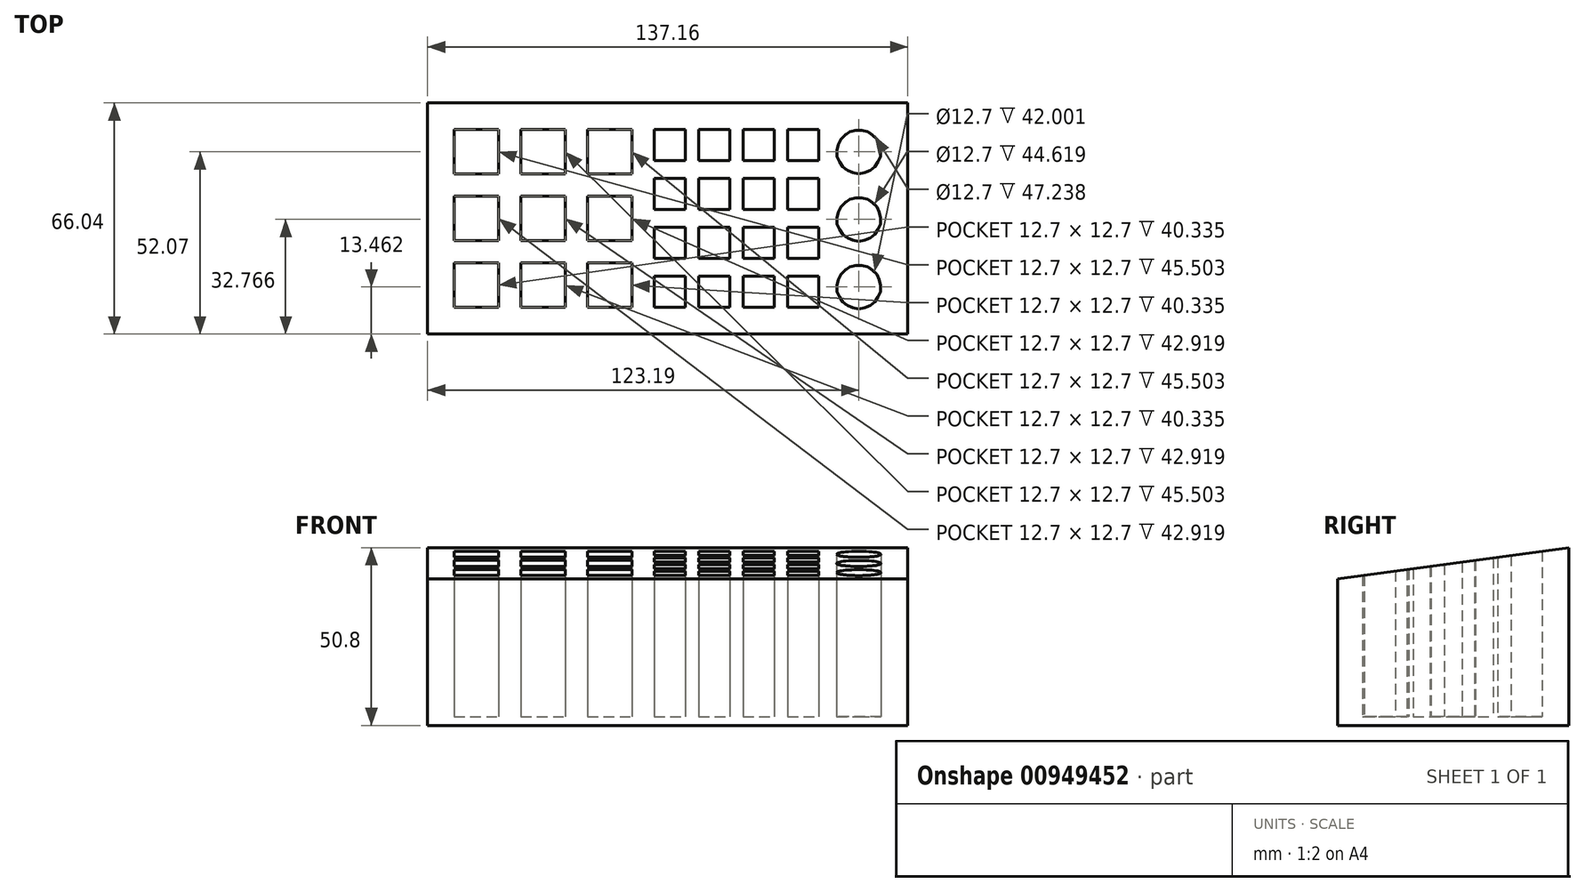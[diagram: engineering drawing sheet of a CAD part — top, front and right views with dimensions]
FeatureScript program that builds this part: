
annotation { "Feature Type Name" : "Feature", "Feature Type Description" : "" }
export const myFeature = defineFeature(function(context is Context, id is Id, definition is map)
    precondition{}
    {
        {
            var Q0;
            Q0=qCreatedBy(makeId("Top.planeOp"),FACE);
            var sketch = newSketch(context, id + "F0", { "sketchPlane" : qUnion([Q0])});
            skLineSegment(sketch, "E0.bottom", {"start": v(-57.15, 6.35) * mm, "end": v(-44.45, 6.35) * mm});
            skLineSegment(sketch, "E0.top", {"start": v(-57.15, -6.35) * mm, "end": v(-44.45, -6.35) * mm});
            skLineSegment(sketch, "E0.left", {"start": v(-57.15, 6.35) * mm, "end": v(-57.15, -6.35) * mm});
            skLineSegment(sketch, "E0.right", {"start": v(-44.45, 6.35) * mm, "end": v(-44.45, -6.35) * mm});
            skPoint(sketch, "E0.middle", {"position": v(-50.8, 0) * mm});
            skLineSegment(sketch, "E1.0.1.0", {"start": v(-57.15, -12.7) * mm, "end": v(-44.45, -12.7) * mm});
            skLineSegment(sketch, "E1.0.1.1", {"start": v(-57.15, -12.7) * mm, "end": v(-57.15, -25.4) * mm});
            skLineSegment(sketch, "E1.0.1.2", {"start": v(-57.15, -25.4) * mm, "end": v(-44.45, -25.4) * mm});
            skLineSegment(sketch, "E1.0.1.3", {"start": v(-44.45, -12.7) * mm, "end": v(-44.45, -25.4) * mm});
            skLineSegment(sketch, "E1.0.2.0", {"start": v(-57.15, -31.75) * mm, "end": v(-44.45, -31.75) * mm});
            skLineSegment(sketch, "E1.0.2.1", {"start": v(-57.15, -31.75) * mm, "end": v(-57.15, -44.45) * mm});
            skLineSegment(sketch, "E1.0.2.2", {"start": v(-57.15, -44.45) * mm, "end": v(-44.45, -44.45) * mm});
            skLineSegment(sketch, "E1.0.2.3", {"start": v(-44.45, -31.75) * mm, "end": v(-44.45, -44.45) * mm});
            skLineSegment(sketch, "E1.1.0.0", {"start": v(-38.1, 6.35) * mm, "end": v(-25.4, 6.35) * mm});
            skLineSegment(sketch, "E1.1.0.1", {"start": v(-38.1, 6.35) * mm, "end": v(-38.1, -6.35) * mm});
            skLineSegment(sketch, "E1.1.0.2", {"start": v(-38.1, -6.35) * mm, "end": v(-25.4, -6.35) * mm});
            skLineSegment(sketch, "E1.1.0.3", {"start": v(-25.4, 6.35) * mm, "end": v(-25.4, -6.35) * mm});
            skLineSegment(sketch, "E1.1.1.0", {"start": v(-38.1, -12.7) * mm, "end": v(-25.4, -12.7) * mm});
            skLineSegment(sketch, "E1.1.1.1", {"start": v(-38.1, -12.7) * mm, "end": v(-38.1, -25.4) * mm});
            skLineSegment(sketch, "E1.1.1.2", {"start": v(-38.1, -25.4) * mm, "end": v(-25.4, -25.4) * mm});
            skLineSegment(sketch, "E1.1.1.3", {"start": v(-25.4, -12.7) * mm, "end": v(-25.4, -25.4) * mm});
            skLineSegment(sketch, "E1.1.2.0", {"start": v(-38.1, -31.75) * mm, "end": v(-25.4, -31.75) * mm});
            skLineSegment(sketch, "E1.1.2.1", {"start": v(-38.1, -31.75) * mm, "end": v(-38.1, -44.45) * mm});
            skLineSegment(sketch, "E1.1.2.2", {"start": v(-38.1, -44.45) * mm, "end": v(-25.4, -44.45) * mm});
            skLineSegment(sketch, "E1.1.2.3", {"start": v(-25.4, -31.75) * mm, "end": v(-25.4, -44.45) * mm});
            skLineSegment(sketch, "E1.2.0.0", {"start": v(-19.05, 6.35) * mm, "end": v(-6.35, 6.35) * mm});
            skLineSegment(sketch, "E1.2.0.1", {"start": v(-19.05, 6.35) * mm, "end": v(-19.05, -6.35) * mm});
            skLineSegment(sketch, "E1.2.0.2", {"start": v(-19.05, -6.35) * mm, "end": v(-6.35, -6.35) * mm});
            skLineSegment(sketch, "E1.2.0.3", {"start": v(-6.35, 6.35) * mm, "end": v(-6.35, -6.35) * mm});
            skLineSegment(sketch, "E1.2.1.0", {"start": v(-19.05, -12.7) * mm, "end": v(-6.35, -12.7) * mm});
            skLineSegment(sketch, "E1.2.1.1", {"start": v(-19.05, -12.7) * mm, "end": v(-19.05, -25.4) * mm});
            skLineSegment(sketch, "E1.2.1.2", {"start": v(-19.05, -25.4) * mm, "end": v(-6.35, -25.4) * mm});
            skLineSegment(sketch, "E1.2.1.3", {"start": v(-6.35, -12.7) * mm, "end": v(-6.35, -25.4) * mm});
            skLineSegment(sketch, "E1.2.2.0", {"start": v(-19.05, -31.75) * mm, "end": v(-6.35, -31.75) * mm});
            skLineSegment(sketch, "E1.2.2.1", {"start": v(-19.05, -31.75) * mm, "end": v(-19.05, -44.45) * mm});
            skLineSegment(sketch, "E1.2.2.2", {"start": v(-19.05, -44.45) * mm, "end": v(-6.35, -44.45) * mm});
            skLineSegment(sketch, "E1.2.2.3", {"start": v(-6.35, -31.75) * mm, "end": v(-6.35, -44.45) * mm});
            skLineSegment(sketch, "E1.direction1", {"start": v(-57.15, 6.35) * mm, "end": v(-38.1, 6.35) * mm, "construction": true});
            skLineSegment(sketch, "E1.direction2", {"start": v(-57.15, 6.35) * mm, "end": v(-57.15, -12.7) * mm, "construction": true});
            skLineSegment(sketch, "E2.bottom", {"start": v(0, -44.45) * mm, "end": v(8.9, -44.45) * mm});
            skLineSegment(sketch, "E2.top", {"start": v(0, -35.56) * mm, "end": v(8.89, -35.56) * mm});
            skLineSegment(sketch, "E2.left", {"start": v(0, -44.45) * mm, "end": v(0, -35.56) * mm});
            skLineSegment(sketch, "E2.right", {"start": v(8.9, -44.45) * mm, "end": v(8.89, -35.56) * mm});
            skLineSegment(sketch, "E3.0.1.0", {"start": v(0, -30.48) * mm, "end": v(0, -21.59) * mm});
            skLineSegment(sketch, "E3.0.1.1", {"start": v(0, -30.48) * mm, "end": v(8.9, -30.48) * mm});
            skLineSegment(sketch, "E3.0.1.2", {"start": v(8.9, -30.48) * mm, "end": v(8.89, -21.59) * mm});
            skLineSegment(sketch, "E3.0.1.3", {"start": v(0, -21.59) * mm, "end": v(8.89, -21.59) * mm});
            skLineSegment(sketch, "E3.0.2.0", {"start": v(0, -16.5) * mm, "end": v(0, -7.62) * mm});
            skLineSegment(sketch, "E3.0.2.1", {"start": v(0, -16.5) * mm, "end": v(8.9, -16.5) * mm});
            skLineSegment(sketch, "E3.0.2.2", {"start": v(8.9, -16.51) * mm, "end": v(8.89, -7.62) * mm});
            skLineSegment(sketch, "E3.0.2.3", {"start": v(0, -7.62) * mm, "end": v(8.89, -7.62) * mm});
            skLineSegment(sketch, "E3.0.3.0", {"start": v(0, -2.54) * mm, "end": v(0, 6.35) * mm});
            skLineSegment(sketch, "E3.0.3.1", {"start": v(0, -2.54) * mm, "end": v(8.9, -2.54) * mm});
            skLineSegment(sketch, "E3.0.3.2", {"start": v(8.9, -2.54) * mm, "end": v(8.89, 6.35) * mm});
            skLineSegment(sketch, "E3.0.3.3", {"start": v(0, 6.35) * mm, "end": v(8.89, 6.35) * mm});
            skLineSegment(sketch, "E3.1.0.0", {"start": v(12.7, -44.45) * mm, "end": v(12.7, -35.56) * mm});
            skLineSegment(sketch, "E3.1.0.1", {"start": v(12.7, -44.45) * mm, "end": v(21.59, -44.45) * mm});
            skLineSegment(sketch, "E3.1.0.2", {"start": v(21.59, -44.45) * mm, "end": v(21.59, -35.56) * mm});
            skLineSegment(sketch, "E3.1.0.3", {"start": v(12.7, -35.56) * mm, "end": v(21.59, -35.56) * mm});
            skLineSegment(sketch, "E3.1.1.0", {"start": v(12.7, -30.48) * mm, "end": v(12.7, -21.59) * mm});
            skLineSegment(sketch, "E3.1.1.1", {"start": v(12.7, -30.48) * mm, "end": v(21.59, -30.48) * mm});
            skLineSegment(sketch, "E3.1.1.2", {"start": v(21.59, -30.48) * mm, "end": v(21.59, -21.59) * mm});
            skLineSegment(sketch, "E3.1.1.3", {"start": v(12.7, -21.59) * mm, "end": v(21.59, -21.59) * mm});
            skLineSegment(sketch, "E3.1.2.0", {"start": v(12.7, -16.5) * mm, "end": v(12.7, -7.62) * mm});
            skLineSegment(sketch, "E3.1.2.1", {"start": v(12.7, -16.5) * mm, "end": v(21.59, -16.5) * mm});
            skLineSegment(sketch, "E3.1.2.2", {"start": v(21.59, -16.51) * mm, "end": v(21.59, -7.62) * mm});
            skLineSegment(sketch, "E3.1.2.3", {"start": v(12.7, -7.62) * mm, "end": v(21.59, -7.62) * mm});
            skLineSegment(sketch, "E3.1.3.0", {"start": v(12.7, -2.54) * mm, "end": v(12.7, 6.35) * mm});
            skLineSegment(sketch, "E3.1.3.1", {"start": v(12.7, -2.54) * mm, "end": v(21.59, -2.54) * mm});
            skLineSegment(sketch, "E3.1.3.2", {"start": v(21.59, -2.54) * mm, "end": v(21.59, 6.35) * mm});
            skLineSegment(sketch, "E3.1.3.3", {"start": v(12.7, 6.35) * mm, "end": v(21.59, 6.35) * mm});
            skLineSegment(sketch, "E3.2.0.0", {"start": v(25.4, -44.45) * mm, "end": v(25.4, -35.56) * mm});
            skLineSegment(sketch, "E3.2.0.1", {"start": v(25.4, -44.45) * mm, "end": v(34.3, -44.45) * mm});
            skLineSegment(sketch, "E3.2.0.2", {"start": v(34.3, -44.45) * mm, "end": v(34.3, -35.56) * mm});
            skLineSegment(sketch, "E3.2.0.3", {"start": v(25.4, -35.56) * mm, "end": v(34.3, -35.56) * mm});
            skLineSegment(sketch, "E3.2.1.0", {"start": v(25.4, -30.48) * mm, "end": v(25.4, -21.59) * mm});
            skLineSegment(sketch, "E3.2.1.1", {"start": v(25.4, -30.48) * mm, "end": v(34.29, -30.48) * mm});
            skLineSegment(sketch, "E3.2.1.2", {"start": v(34.3, -30.48) * mm, "end": v(34.3, -21.59) * mm});
            skLineSegment(sketch, "E3.2.1.3", {"start": v(25.4, -21.59) * mm, "end": v(34.29, -21.59) * mm});
            skLineSegment(sketch, "E3.2.2.0", {"start": v(25.4, -16.5) * mm, "end": v(25.4, -7.62) * mm});
            skLineSegment(sketch, "E3.2.2.1", {"start": v(25.4, -16.5) * mm, "end": v(34.29, -16.5) * mm});
            skLineSegment(sketch, "E3.2.2.2", {"start": v(34.3, -16.51) * mm, "end": v(34.3, -7.62) * mm});
            skLineSegment(sketch, "E3.2.2.3", {"start": v(25.4, -7.62) * mm, "end": v(34.29, -7.62) * mm});
            skLineSegment(sketch, "E3.2.3.0", {"start": v(25.4, -2.54) * mm, "end": v(25.4, 6.35) * mm});
            skLineSegment(sketch, "E3.2.3.1", {"start": v(25.4, -2.54) * mm, "end": v(34.29, -2.54) * mm});
            skLineSegment(sketch, "E3.2.3.2", {"start": v(34.3, -2.54) * mm, "end": v(34.3, 6.35) * mm});
            skLineSegment(sketch, "E3.2.3.3", {"start": v(25.4, 6.35) * mm, "end": v(34.29, 6.35) * mm});
            skLineSegment(sketch, "E3.3.0.0", {"start": v(38.1, -44.45) * mm, "end": v(38.1, -35.56) * mm});
            skLineSegment(sketch, "E3.3.0.1", {"start": v(38.1, -44.45) * mm, "end": v(47, -44.45) * mm});
            skLineSegment(sketch, "E3.3.0.2", {"start": v(47, -44.45) * mm, "end": v(47, -35.56) * mm});
            skLineSegment(sketch, "E3.3.0.3", {"start": v(38.1, -35.56) * mm, "end": v(46.99, -35.56) * mm});
            skLineSegment(sketch, "E3.3.1.0", {"start": v(38.1, -30.48) * mm, "end": v(38.1, -21.59) * mm});
            skLineSegment(sketch, "E3.3.1.1", {"start": v(38.1, -30.48) * mm, "end": v(46.99, -30.48) * mm});
            skLineSegment(sketch, "E3.3.1.2", {"start": v(47, -30.48) * mm, "end": v(47, -21.59) * mm});
            skLineSegment(sketch, "E3.3.1.3", {"start": v(38.1, -21.59) * mm, "end": v(46.99, -21.59) * mm});
            skLineSegment(sketch, "E3.3.2.0", {"start": v(38.1, -16.5) * mm, "end": v(38.1, -7.62) * mm});
            skLineSegment(sketch, "E3.3.2.1", {"start": v(38.1, -16.5) * mm, "end": v(46.99, -16.5) * mm});
            skLineSegment(sketch, "E3.3.2.2", {"start": v(47, -16.51) * mm, "end": v(47, -7.62) * mm});
            skLineSegment(sketch, "E3.3.2.3", {"start": v(38.1, -7.62) * mm, "end": v(46.99, -7.62) * mm});
            skLineSegment(sketch, "E3.3.3.0", {"start": v(38.1, -2.54) * mm, "end": v(38.1, 6.35) * mm});
            skLineSegment(sketch, "E3.3.3.1", {"start": v(38.1, -2.54) * mm, "end": v(46.99, -2.54) * mm});
            skLineSegment(sketch, "E3.3.3.2", {"start": v(47, -2.54) * mm, "end": v(47, 6.35) * mm});
            skLineSegment(sketch, "E3.3.3.3", {"start": v(38.1, 6.35) * mm, "end": v(46.99, 6.35) * mm});
            skLineSegment(sketch, "E3.direction1", {"start": v(0, -44.45) * mm, "end": v(12.7, -44.45) * mm, "construction": true});
            skLineSegment(sketch, "E3.direction2", {"start": v(0, -44.45) * mm, "end": v(0, -30.48) * mm, "construction": true});
            skCircle(sketch, "E4", {"center": v(58.42, 0) * mm, "radius": 6.35 * mm});
            skCircle(sketch, "E5.0.1.0", {"center": v(58.42, -19.3) * mm, "radius": 6.35 * mm});
            skCircle(sketch, "E5.0.2.0", {"center": v(58.42, -38.6) * mm, "radius": 6.35 * mm});
            skLineSegment(sketch, "E5.direction1", {"start": v(58.42, 0) * mm, "end": v(78.43, 0) * mm, "construction": true});
            skLineSegment(sketch, "E5.direction2", {"start": v(58.42, 0) * mm, "end": v(58.42, -19.3) * mm, "construction": true});
            skLineSegment(sketch, "E6.bottom", {"start": v(-64.77, 13.97) * mm, "end": v(72.39, 13.97) * mm});
            skLineSegment(sketch, "E6.top", {"start": v(-64.77, -52.07) * mm, "end": v(72.39, -52.07) * mm});
            skLineSegment(sketch, "E6.left", {"start": v(-64.77, 13.97) * mm, "end": v(-64.77, -52.07) * mm});
            skLineSegment(sketch, "E6.right", {"start": v(72.39, 13.97) * mm, "end": v(72.39, -52.07) * mm});
            skSolve(sketch);
        }
        {
            var Q0;
            Q0=makeQuery(id+"F0.imprint","IMPRINT",FACE,{"disambiguationData":[TD([[makeQuery(id+"F0.imprint","IMPRINT",EDGE,{"derivedFrom":sQuery(id+"F0.wireOp",EDGE,"E0.bottom")}),1.0]])]});
            extrude(context, id + "F1", {"entities" : qUnion([Q0]), "depth" : 50.8 * mm, "offsetDistance" : 25.4 * mm});
        }
        {
            var Q0;
            Q0=makeQuery(id+"F0.imprint","IMPRINT",FACE,{"disambiguationData":[TD([[makeQuery(id+"F0.imprint","IMPRINT",EDGE,{"derivedFrom":sQuery(id+"F0.wireOp",EDGE,"E0.bottom")}),-1.0]])]});
            var Q1;
            Q1=makeQuery(id+"F0.imprint","IMPRINT",FACE,{"disambiguationData":[TD([[makeQuery(id+"F0.imprint","IMPRINT",EDGE,{"derivedFrom":sQuery(id+"F0.wireOp",EDGE,"E1.1.0.0")}),-1.0]])]});
            var Q2;
            Q2=makeQuery(id+"F0.imprint","IMPRINT",FACE,{"disambiguationData":[TD([[makeQuery(id+"F0.imprint","IMPRINT",EDGE,{"derivedFrom":sQuery(id+"F0.wireOp",EDGE,"E1.0.1.0")}),-1.0]])]});
            var Q3;
            Q3=makeQuery(id+"F0.imprint","IMPRINT",FACE,{"disambiguationData":[TD([[makeQuery(id+"F0.imprint","IMPRINT",EDGE,{"derivedFrom":sQuery(id+"F0.wireOp",EDGE,"E1.1.1.0")}),-1.0]])]});
            var Q4;
            Q4=makeQuery(id+"F0.imprint","IMPRINT",FACE,{"disambiguationData":[TD([[makeQuery(id+"F0.imprint","IMPRINT",EDGE,{"derivedFrom":sQuery(id+"F0.wireOp",EDGE,"E1.0.2.0")}),-1.0]])]});
            var Q5;
            Q5=makeQuery(id+"F0.imprint","IMPRINT",FACE,{"disambiguationData":[TD([[makeQuery(id+"F0.imprint","IMPRINT",EDGE,{"derivedFrom":sQuery(id+"F0.wireOp",EDGE,"E1.1.2.0")}),-1.0]])]});
            var Q6;
            Q6=makeQuery(id+"F0.imprint","IMPRINT",FACE,{"disambiguationData":[TD([[makeQuery(id+"F0.imprint","IMPRINT",EDGE,{"derivedFrom":sQuery(id+"F0.wireOp",EDGE,"E1.2.2.0")}),-1.0]])]});
            var Q7;
            Q7=makeQuery(id+"F0.imprint","IMPRINT",FACE,{"disambiguationData":[TD([[makeQuery(id+"F0.imprint","IMPRINT",EDGE,{"derivedFrom":sQuery(id+"F0.wireOp",EDGE,"E1.2.1.0")}),-1.0]])]});
            var Q8;
            Q8=makeQuery(id+"F0.imprint","IMPRINT",FACE,{"disambiguationData":[TD([[makeQuery(id+"F0.imprint","IMPRINT",EDGE,{"derivedFrom":sQuery(id+"F0.wireOp",EDGE,"E1.2.0.0")}),-1.0]])]});
            var Q9;
            Q9=makeQuery(id+"F0.imprint","IMPRINT",FACE,{"disambiguationData":[TD([[makeQuery(id+"F0.imprint","IMPRINT",EDGE,{"derivedFrom":sQuery(id+"F0.wireOp",EDGE,"E3.0.3.0")}),-1.0]])]});
            var Q10;
            Q10=makeQuery(id+"F0.imprint","IMPRINT",FACE,{"disambiguationData":[TD([[makeQuery(id+"F0.imprint","IMPRINT",EDGE,{"derivedFrom":sQuery(id+"F0.wireOp",EDGE,"E3.0.2.0")}),-1.0]])]});
            var Q11;
            Q11=makeQuery(id+"F0.imprint","IMPRINT",FACE,{"disambiguationData":[TD([[makeQuery(id+"F0.imprint","IMPRINT",EDGE,{"derivedFrom":sQuery(id+"F0.wireOp",EDGE,"E3.0.1.0")}),-1.0]])]});
            var Q12;
            Q12=makeQuery(id+"F0.imprint","IMPRINT",FACE,{"disambiguationData":[TD([[makeQuery(id+"F0.imprint","IMPRINT",EDGE,{"derivedFrom":sQuery(id+"F0.wireOp",EDGE,"E2.bottom")}),1.0]])]});
            var Q13;
            Q13=makeQuery(id+"F0.imprint","IMPRINT",FACE,{"disambiguationData":[TD([[makeQuery(id+"F0.imprint","IMPRINT",EDGE,{"derivedFrom":sQuery(id+"F0.wireOp",EDGE,"E3.1.0.0")}),-1.0]])]});
            var Q14;
            Q14=makeQuery(id+"F0.imprint","IMPRINT",FACE,{"disambiguationData":[TD([[makeQuery(id+"F0.imprint","IMPRINT",EDGE,{"derivedFrom":sQuery(id+"F0.wireOp",EDGE,"E3.1.1.0")}),-1.0]])]});
            var Q15;
            Q15=makeQuery(id+"F0.imprint","IMPRINT",FACE,{"disambiguationData":[TD([[makeQuery(id+"F0.imprint","IMPRINT",EDGE,{"derivedFrom":sQuery(id+"F0.wireOp",EDGE,"E3.1.2.0")}),-1.0]])]});
            var Q16;
            Q16=makeQuery(id+"F0.imprint","IMPRINT",FACE,{"disambiguationData":[TD([[makeQuery(id+"F0.imprint","IMPRINT",EDGE,{"derivedFrom":sQuery(id+"F0.wireOp",EDGE,"E3.1.3.0")}),-1.0]])]});
            var Q17;
            Q17=makeQuery(id+"F0.imprint","IMPRINT",FACE,{"disambiguationData":[TD([[makeQuery(id+"F0.imprint","IMPRINT",EDGE,{"derivedFrom":sQuery(id+"F0.wireOp",EDGE,"E3.2.3.0")}),-1.0]])]});
            var Q18;
            Q18=makeQuery(id+"F0.imprint","IMPRINT",FACE,{"disambiguationData":[TD([[makeQuery(id+"F0.imprint","IMPRINT",EDGE,{"derivedFrom":sQuery(id+"F0.wireOp",EDGE,"E3.3.3.0")}),-1.0]])]});
            var Q19;
            Q19=makeQuery(id+"F0.imprint","IMPRINT",FACE,{"disambiguationData":[TD([[makeQuery(id+"F0.imprint","IMPRINT",EDGE,{"derivedFrom":sQuery(id+"F0.wireOp",EDGE,"E3.3.2.0")}),-1.0]])]});
            var Q20;
            Q20=makeQuery(id+"F0.imprint","IMPRINT",FACE,{"disambiguationData":[TD([[makeQuery(id+"F0.imprint","IMPRINT",EDGE,{"derivedFrom":sQuery(id+"F0.wireOp",EDGE,"E3.2.2.0")}),-1.0]])]});
            var Q21;
            Q21=makeQuery(id+"F0.imprint","IMPRINT",FACE,{"disambiguationData":[TD([[makeQuery(id+"F0.imprint","IMPRINT",EDGE,{"derivedFrom":sQuery(id+"F0.wireOp",EDGE,"E3.2.1.0")}),-1.0]])]});
            var Q22;
            Q22=makeQuery(id+"F0.imprint","IMPRINT",FACE,{"disambiguationData":[TD([[makeQuery(id+"F0.imprint","IMPRINT",EDGE,{"derivedFrom":sQuery(id+"F0.wireOp",EDGE,"E3.3.1.0")}),-1.0]])]});
            var Q23;
            Q23=makeQuery(id+"F0.imprint","IMPRINT",FACE,{"disambiguationData":[TD([[makeQuery(id+"F0.imprint","IMPRINT",EDGE,{"derivedFrom":sQuery(id+"F0.wireOp",EDGE,"E3.2.0.0")}),-1.0]])]});
            var Q24;
            Q24=makeQuery(id+"F0.imprint","IMPRINT",FACE,{"disambiguationData":[TD([[makeQuery(id+"F0.imprint","IMPRINT",EDGE,{"derivedFrom":sQuery(id+"F0.wireOp",EDGE,"E3.3.0.0")}),-1.0]])]});
            var Q25;
            Q25=makeQuery(id+"F0.imprint","IMPRINT",FACE,{"disambiguationData":[TD([[makeQuery(id+"F0.imprint","IMPRINT",EDGE,{"derivedFrom":sQuery(id+"F0.wireOp",EDGE,"E5.0.2.0")}),1.0]])]});
            var Q26;
            Q26=makeQuery(id+"F0.imprint","IMPRINT",FACE,{"disambiguationData":[TD([[makeQuery(id+"F0.imprint","IMPRINT",EDGE,{"derivedFrom":sQuery(id+"F0.wireOp",EDGE,"E5.0.1.0")}),1.0]])]});
            var Q27;
            Q27=makeQuery(id+"F0.imprint","IMPRINT",FACE,{"disambiguationData":[TD([[makeQuery(id+"F0.imprint","IMPRINT",EDGE,{"derivedFrom":sQuery(id+"F0.wireOp",EDGE,"E4")}),1.0]])]});
            extrude(context, id + "F2", {"entities" : qUnion([Q0, Q1, Q2, Q3, Q4, Q5, Q6, Q7, Q8, Q9, Q10, Q11, Q12, Q13, Q14, Q15, Q16, Q17, Q18, Q19, Q20, Q21, Q22, Q23, Q24, Q25, Q26, Q27]), "operationType" : NewBodyOperationType.ADD, "depth" : 2.54 * mm, "offsetDistance" : 25.4 * mm});
        }
        {
            var Q0;
            Q0=makeQuery(id+"F1.opExtrude","SWEPT_FACE",FACE,{"disambiguationData":[OSD([sQuery(id+"F0.wireOp",EDGE,"E6.left")])]});
            var sketch = newSketch(context, id + "F3", { "sketchPlane" : qUnion([Q0])});
            skLineSegment(sketch, "E7", {"start": v(-13.97, 50.8) * mm, "end": v(52.07, 41.84) * mm});
            skLineSegment(sketch, "E8", {"start": v(52.07, 41.84) * mm, "end": v(52.07, 50.8) * mm});
            skLineSegment(sketch, "E9", {"start": v(52.07, 50.8) * mm, "end": v(-13.97, 50.8) * mm});
            skSolve(sketch);
        }
        {
            var Q0;
            Q0=makeQuery(id+"F3.imprint","IMPRINT",FACE,{"disambiguationData":[TD([[makeQuery(id+"F3.imprint","IMPRINT",EDGE,{"derivedFrom":sQuery(id+"F3.wireOp",EDGE,"E7")}),1.0]])]});
            extrude(context, id + "F4", {"entities" : qUnion([Q0]), "operationType" : NewBodyOperationType.REMOVE, "oppositeDirection" : true, "depth" : 149.1 * mm, "offsetDistance" : 25.4 * mm});
        }
    });
